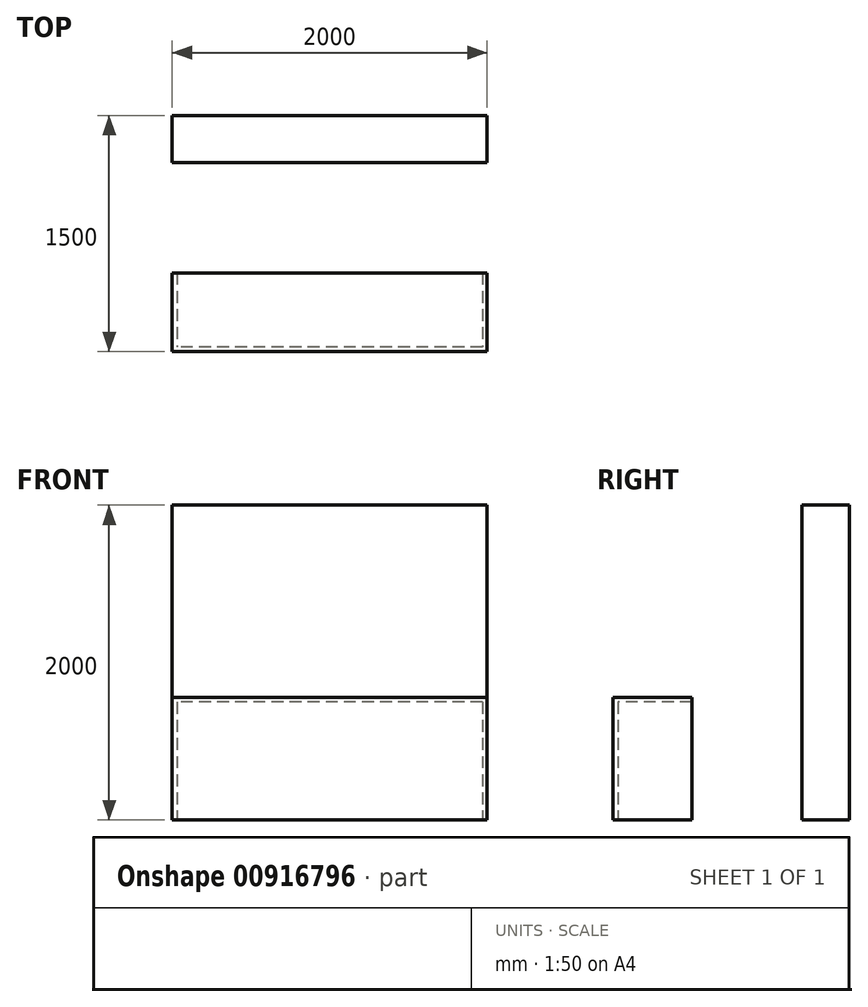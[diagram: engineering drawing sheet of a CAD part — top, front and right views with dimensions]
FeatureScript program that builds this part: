
annotation { "Feature Type Name" : "Feature", "Feature Type Description" : "" }
export const myFeature = defineFeature(function(context is Context, id is Id, definition is map)
    precondition{}
    {
        {
            var Q0;
            Q0=qCreatedBy(makeId("Top.planeOp"),FACE);
            var sketch = newSketch(context, id + "F0", { "sketchPlane" : qUnion([Q0])});
            skLineSegment(sketch, "E0.bottom", {"start": v(1000, 750) * mm, "end": v(-1000, 750) * mm});
            skLineSegment(sketch, "E0.top", {"start": v(1000, -750) * mm, "end": v(-1000, -750) * mm});
            skLineSegment(sketch, "E0.left", {"start": v(1000, 750) * mm, "end": v(1000, -750) * mm});
            skLineSegment(sketch, "E0.right", {"start": v(-1000, 750) * mm, "end": v(-1000, -750) * mm});
            skPoint(sketch, "E0.middle", {"position": v(0, 0) * mm});
            skLineSegment(sketch, "E1", {"start": v(-1000, -250) * mm, "end": v(1000, -250) * mm});
            skLineSegment(sketch, "E2", {"start": v(-1000, 450) * mm, "end": v(1000, 450) * mm});
            skSolve(sketch);
        }
        {
            var Q0;
            Q0=qCreatedBy(makeId("Top.planeOp"),FACE);
            var sketch = newSketch(context, id + "F1", { "sketchPlane" : qUnion([Q0])});
            skLineSegment(sketch, "E3.0", {"start": v(1000, 750) * mm, "end": v(-1000, 750) * mm});
            skLineSegment(sketch, "E3.1", {"start": v(-1000, 450) * mm, "end": v(1000, 450) * mm});
            skLineSegment(sketch, "E3.2", {"start": v(1000, 750) * mm, "end": v(1000, 450) * mm});
            skLineSegment(sketch, "E3.3", {"start": v(-1000, 750) * mm, "end": v(-1000, 450) * mm});
            skPoint(sketch, "E4.orphan", {"position": v(-1000, -750) * mm});
            skPoint(sketch, "E5.orphan", {"position": v(1000, -750) * mm});
            skSolve(sketch);
        }
        {
            var Q0;
            Q0=qSketchRegion(id+"F1",true);
            extrude(context, id + "F2", {"entities" : qUnion([Q0]), "depth" : 2000 * mm, "offsetDistance" : 25 * mm});
        }
        {
            var Q0;
            Q0=qCreatedBy(makeId("Top.planeOp"),FACE);
            var sketch = newSketch(context, id + "F3", { "sketchPlane" : qUnion([Q0])});
            skLineSegment(sketch, "E6.0", {"start": v(1000, -250) * mm, "end": v(1000, -750) * mm});
            skLineSegment(sketch, "E6.1", {"start": v(1000, -750) * mm, "end": v(-1000, -750) * mm});
            skLineSegment(sketch, "E6.2", {"start": v(-1000, -250) * mm, "end": v(-1000, -750) * mm});
            skLineSegment(sketch, "E7.0", {"start": v(-970, -250) * mm, "end": v(-970, -720) * mm});
            skLineSegment(sketch, "E7.1", {"start": v(970, -720) * mm, "end": v(-970, -720) * mm});
            skLineSegment(sketch, "E7.2", {"start": v(970, -250) * mm, "end": v(970, -720) * mm});
            skLineSegment(sketch, "E8", {"start": v(-1000, -250) * mm, "end": v(-970, -250) * mm});
            skLineSegment(sketch, "E9", {"start": v(970, -250) * mm, "end": v(1000, -250) * mm});
            skSolve(sketch);
        }
        {
            var Q0;
            Q0=qSketchRegion(id+"F3",true);
            extrude(context, id + "F4", {"entities" : qUnion([Q0]), "operationType" : NewBodyOperationType.ADD, "depth" : 750 * mm, "offsetDistance" : 25 * mm});
        }
        {
            var Q0;
            Q0=makeQuery(id+"F4.opExtrude","CAP_FACE",FACE,{"disambiguationData":[OSD([sQuery(id+"F3.wireOp",EDGE,"E6.0"),sQuery(id+"F3.wireOp",EDGE,"E6.1"),sQuery(id+"F3.wireOp",EDGE,"E6.2"),sQuery(id+"F3.wireOp",EDGE,"E7.0"),sQuery(id+"F3.wireOp",EDGE,"E7.1"),sQuery(id+"F3.wireOp",EDGE,"E7.2"),sQuery(id+"F3.wireOp",EDGE,"mYHOJCN0-04EG-1qpz-t4CE-P64e15eP6tz6"),sQuery(id+"F3.wireOp",EDGE,"E8")])],"isStart":false});
            var sketch = newSketch(context, id + "F5", { "sketchPlane" : qUnion([Q0])});
            skLineSegment(sketch, "E10.0", {"start": v(-1000, -250) * mm, "end": v(1000, -250) * mm});
            skLineSegment(sketch, "E10.1", {"start": v(1000, -250) * mm, "end": v(1000, -750) * mm});
            skLineSegment(sketch, "E10.2", {"start": v(1000, -750) * mm, "end": v(-1000, -750) * mm});
            skLineSegment(sketch, "E10.3", {"start": v(-1000, -250) * mm, "end": v(-1000, -750) * mm});
            skPoint(sketch, "E11.orphan", {"position": v(-1000, 750) * mm});
            skPoint(sketch, "E12.orphan", {"position": v(1000, 750) * mm});
            skSolve(sketch);
        }
        {
            var Q0;
            Q0=qSketchRegion(id+"F5",true);
            extrude(context, id + "F6", {"entities" : qUnion([Q0]), "operationType" : NewBodyOperationType.ADD, "depth" : 30 * mm, "offsetDistance" : 25 * mm});
        }
        {
            var Q0;
            Q0=makeQuery(id+"F2.opExtrude","SWEPT_BODY",BODY,{"disambiguationData":[OSD([sQuery(id+"F1.wireOp",EDGE,"E3.0"),sQuery(id+"F1.wireOp",EDGE,"E3.1"),sQuery(id+"F1.wireOp",EDGE,"E3.2"),sQuery(id+"F1.wireOp",EDGE,"E3.3")])]});
            var Q1;
            Q1=qCreatedBy(makeId("Right.planeOp"),FACE);
            mirror(context, id + "F7", {"entities" : qUnion([Q0]), "mirrorPlane" : qUnion([Q1])});
        }
        {
            var Q0;
            Q0=makeQuery(id+"F7.opPattern","COPY",BODY,{"derivedFrom":makeQuery(id+"F2.opExtrude","SWEPT_BODY",BODY,{"disambiguationData":[OSD([sQuery(id+"F1.wireOp",EDGE,"E3.0"),sQuery(id+"F1.wireOp",EDGE,"E3.1"),sQuery(id+"F1.wireOp",EDGE,"E3.2"),sQuery(id+"F1.wireOp",EDGE,"E3.3")])]}),"instanceName":"1"});
            deleteBodies(context, id + "F8", {"entities" : qUnion([Q0])});
        }
    });
